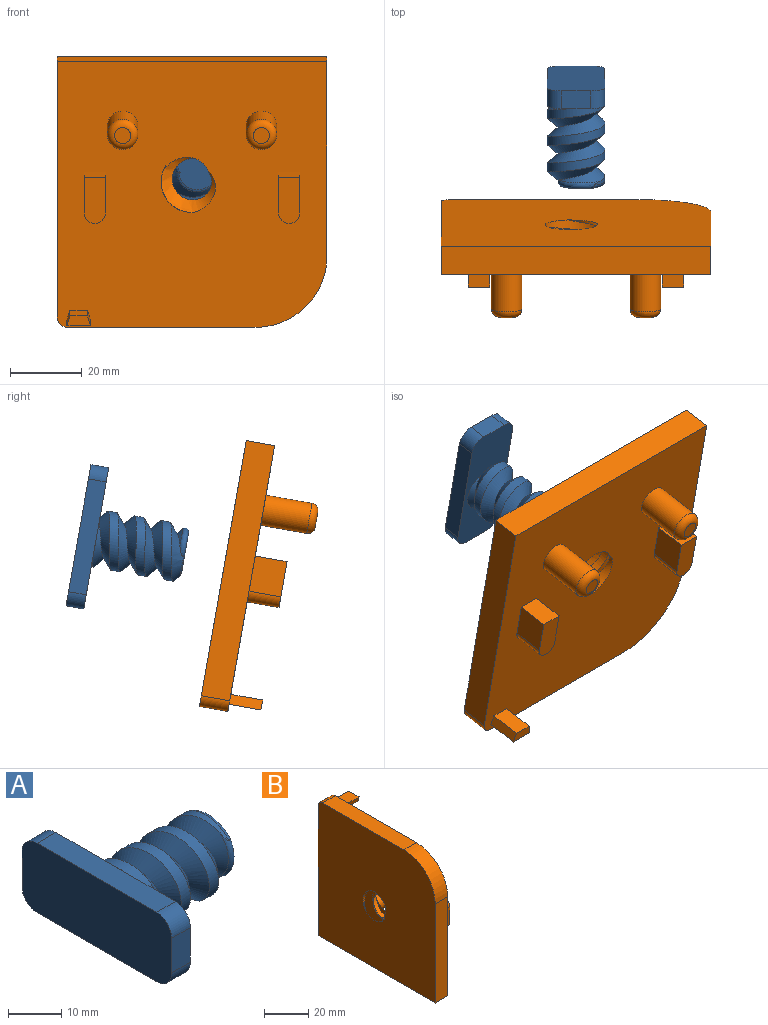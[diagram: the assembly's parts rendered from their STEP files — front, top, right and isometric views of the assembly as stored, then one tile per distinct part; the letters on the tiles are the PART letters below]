
ASSEMBLY  parts=2 mates=1
PART A: 17 faces, bbox 34.8x41.4x18.8 mm
  f0: cylinder r=8mm len=24mm, axis (-1,0,0), area 401.9mm2, adj f1,f2,f5,f14,f15
  f1: bspline ~31.39x16mm, area 534.2mm2, adj f0,f2,f5,f14,f15,f16
  f2: bspline ~28.75x16mm, area 499mm2, adj f0,f1,f5,f15
  f3: plane 11.68x10.95mm, normal (1,0,0), area 101.9mm2, adj f14,f15,f16
  f4: plane 31.85x5mm, normal (0,0,1), area 159.2mm2, adj f5,f11,f12,f13
  f5: plane 41.41x17.56mm, normal (1,0,0), area 466.7mm2, adj f0,f1,f2,f4,f6,f7,f8,f9
  f6: plane 8x5mm, normal (0,1,0), area 40mm2, adj f5,f7,f12,f13
  f7: cylinder r=4mm len=5mm, axis (-1,0,0), area 31.4mm2, adj f5,f6,f8,f13
  f8: plane 31.85x5mm, normal (0,0,-1), area 159.2mm2, adj f5,f7,f9,f13
  f9: cylinder r=4mm len=5mm, axis (-1,0,0), area 31.4mm2, adj f5,f8,f10,f13
  f10: plane 8x5mm, normal (0,-1,0), area 40mm2, adj f5,f9,f11,f13
  f11: cylinder r=4mm len=5mm, axis (-1,0,0), area 31.4mm2, adj f4,f5,f10,f13
  f12: cylinder r=4mm len=5mm, axis (-1,0,0), area 31.4mm2, adj f4,f5,f6,f13
  f13: plane 39.85x16mm, normal (-1,0,0), area 623.8mm2, adj f4,f6,f7,f8,f9,f10,f11,f12
  f14: torus R=7mm, axis (1,0,0), area 17mm2, adj f0,f1,f3,f15,f16
  f15: bspline ~15.87x11.53mm, area 35.3mm2, adj f0,f1,f2,f3,f14,f16
  f16: bspline ~11.23x5.9mm, area 10.2mm2, adj f1,f3,f14,f15
PART B: 31 faces, bbox 27.7x76.6x76.6 mm
  f0: plane 76.64x76.64mm, normal (1,0,0), area 5079.5mm2, adj f2,f3,f4,f5,f6,f7,f8,f9
  f1: plane 76.51x76.51mm, normal (-1,0,0), area 5356.1mm2, adj f2,f3,f4,f5,f6,f7,f25,f26
  f2: cylinder r=20mm len=20mm, axis (-1,0,0), area 251.3mm2, adj f0,f1,f3,f7
  f3: plane 55x8mm, normal (0,-1,0), area 440mm2, adj f0,f1,f2,f4
  f4: plane 75x8mm, normal (0,0,-1), area 600mm2, adj f0,f1,f3,f5
  f5: plane 72x8mm, normal (0,1,0), area 576mm2, adj f0,f1,f4,f6
  f6: cylinder r=3mm len=8mm, axis (-1,0,0), area 37.7mm2, adj f0,f1,f5,f7
  f7: plane 52x8mm, normal (0,0,1), area 416mm2, adj f0,f1,f2,f6
  f8: cylinder r=4.25mm len=13mm, axis (-1,0,0), area 347.1mm2, adj f0,f30
  f9: cylinder r=4.25mm len=13mm, axis (-1,0,0), area 347.1mm2, adj f0,f29
  f10: plane 9.93x9mm, normal (0,1,0), area 89.4mm2, adj f0,f11,f13,f14
  f11: cylinder r=3mm len=9mm, axis (-1,0,0), area 84.8mm2, adj f0,f10,f12,f14
  f12: plane 9.93x9mm, normal (0,-1,0), area 89.4mm2, adj f0,f11,f13,f14
  f13: plane 9x6mm, normal (0,0,-1), area 54mm2, adj f0,f10,f12,f14
  f14: plane 12.93x6mm, normal (1,0,0), area 73.7mm2, adj f10,f11,f12,f13
  f15: plane 9.93x9mm, normal (0,-1,0), area 89.4mm2, adj f0,f16,f18,f19
  f16: plane 9x6mm, normal (0,0,-1), area 54mm2, adj f0,f15,f17,f19
  f17: plane 9.93x9mm, normal (0,1,0), area 89.4mm2, adj f0,f16,f18,f19
  f18: cylinder r=3mm len=9mm, axis (-1,0,0), area 84.8mm2, adj f0,f15,f17,f19
  f19: plane 12.93x6mm, normal (1,0,0), area 73.7mm2, adj f15,f16,f17,f18
  f20: plane 9x2.8mm, normal (0,-0.97,-0.26), area 26.1mm2, adj f0,f21,f23,f24
  f21: plane 9x5mm, normal (0,0,-1), area 45mm2, adj f0,f20,f22,f24
  f22: plane 9x2.8mm, normal (0,0.97,-0.26), area 26.1mm2, adj f0,f21,f23,f24
  f23: plane 9x6.5mm, normal (0,0,1), area 58.5mm2, adj f0,f20,f22,f24
  f24: plane 6.5x2.8mm, normal (1,0,0), area 16.1mm2, adj f20,f21,f22,f23
  f25: cylinder r=8.6mm len=17.2mm, axis (-1,0,0), area 132mm2, adj f0,f1,f26
  f26: bspline ~17.2x17.2mm, area 183.9mm2, adj f0,f1,f25
  f27: plane 4.5x4.5mm, normal (1,0,0), area 15.9mm2, adj f30
  f28: plane 4.5x4.5mm, normal (1,0,0), area 15.9mm2, adj f29
  f29: torus R=2.25mm, axis (1,0,0), area 69.5mm2, adj f9,f28
  f30: torus R=2.25mm, axis (1,0,0), area 69.5mm2, adj f8,f27
PLACE A rot(axis=(-0.54,0.64,-0.54),114.4deg) t=(-21.64,-10.84,3.65)mm
PLACE B rot(axis=(-0.71,0.71,0.06),172.9deg) t=(-25.14,-46.04,-6.11)mm fixed
MATE slider B.f25 <-> A.f0  axis (0,0.98,0.17) through (-25.14,-46.65,-2.66)mm
